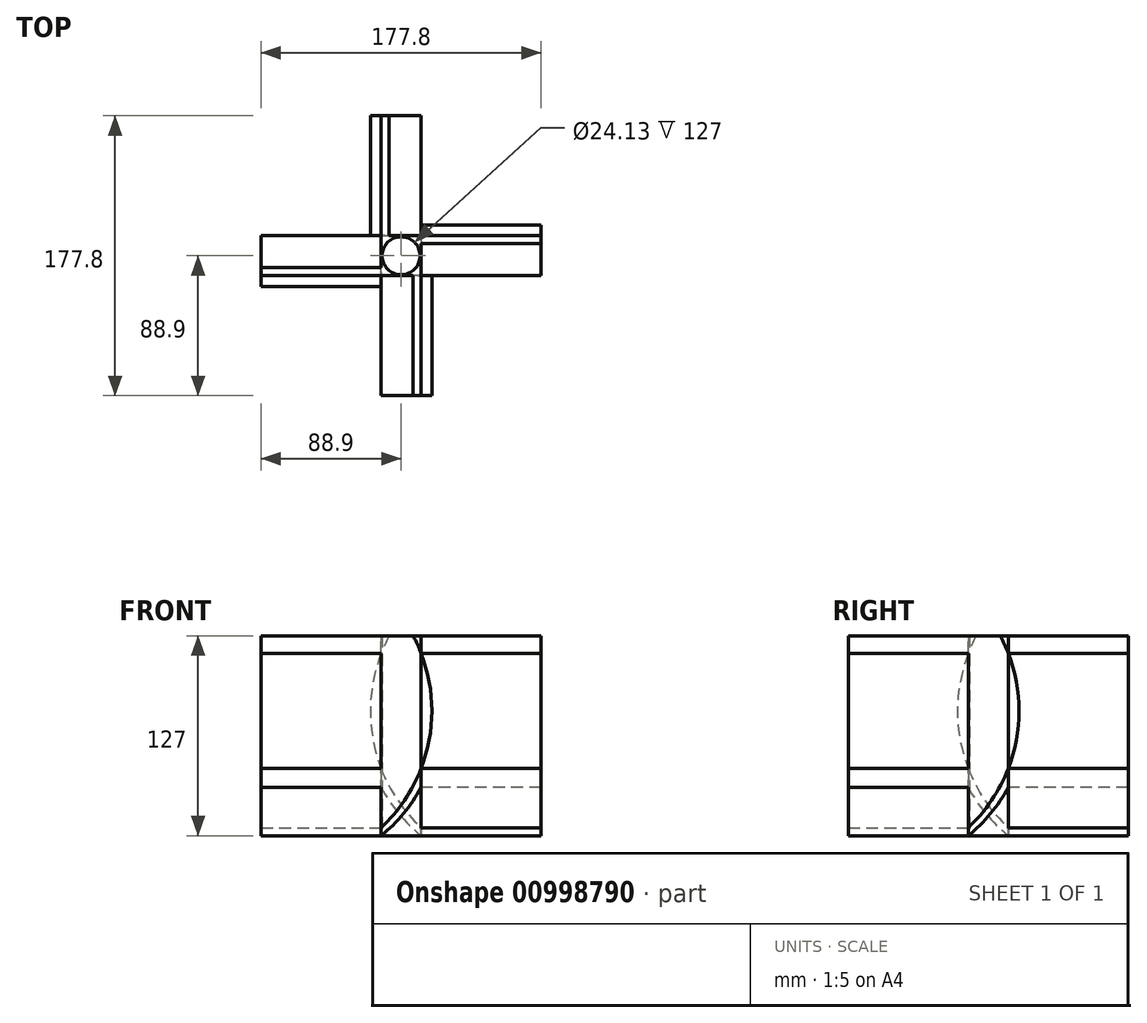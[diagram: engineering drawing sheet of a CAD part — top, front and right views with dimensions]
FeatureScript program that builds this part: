
annotation { "Feature Type Name" : "Feature", "Feature Type Description" : "" }
export const myFeature = defineFeature(function(context is Context, id is Id, definition is map)
    precondition{}
    {
        {
            var Q0;
            Q0=qCreatedBy(makeId("Top.planeOp"),FACE);
            var sketch = newSketch(context, id + "F0", { "sketchPlane" : qUnion([Q0])});
            skCircle(sketch, "E0", {"center": v(0, 0) * mm, "radius": 12.07 * mm});
            skLineSegment(sketch, "E1.bottom", {"start": v(12.7, -12.7) * mm, "end": v(-12.7, -12.7) * mm});
            skLineSegment(sketch, "E1.top", {"start": v(12.7, 12.7) * mm, "end": v(-12.7, 12.7) * mm});
            skLineSegment(sketch, "E1.left", {"start": v(12.7, -12.7) * mm, "end": v(12.7, 12.7) * mm});
            skLineSegment(sketch, "E1.right", {"start": v(-12.7, -12.7) * mm, "end": v(-12.7, 12.7) * mm});
            skSolve(sketch);
        }
        {
            var Q0;
            {var subQ0=sQuery(id+"F0.wireOp",EDGE,"E1.top");var subQ1=sQuery(id+"F0.wireOp",EDGE,"E0");var subQ2=makeQuery(id+"F0.imprint","INTERSECT",VERTEX,{"derivedFrom":[subQ1,subQ0]});Q0=makeQuery(id+"F0.imprint","IMPRINT",FACE,{"disambiguationData":[TD([[makeQuery(id+"F0.imprint","IMPRINT",EDGE,{"disambiguationData":[TD([[subQ2,1.0]])],"derivedFrom":subQ1}),-1.0]])]});}
            var Q1;
            {var subQ0=sQuery(id+"F0.wireOp",EDGE,"E1.top");var subQ1=sQuery(id+"F0.wireOp",EDGE,"E0");var subQ2=makeQuery(id+"F0.imprint","INTERSECT",VERTEX,{"derivedFrom":[subQ1,subQ0]});Q1=makeQuery(id+"F0.imprint","IMPRINT",FACE,{"disambiguationData":[TD([[makeQuery(id+"F0.imprint","IMPRINT",EDGE,{"disambiguationData":[TD([[subQ2,-1.0]])],"derivedFrom":subQ1}),-1.0]])]});}
            var Q2;
            {var subQ0=sQuery(id+"F0.wireOp",EDGE,"E1.right");var subQ1=sQuery(id+"F0.wireOp",EDGE,"E0");var subQ2=makeQuery(id+"F0.imprint","INTERSECT",VERTEX,{"derivedFrom":[subQ1,subQ0]});Q2=makeQuery(id+"F0.imprint","IMPRINT",FACE,{"disambiguationData":[TD([[makeQuery(id+"F0.imprint","IMPRINT",EDGE,{"disambiguationData":[TD([[subQ2,-1.0]])],"derivedFrom":subQ1}),-1.0]])]});}
            var Q3;
            {var subQ0=sQuery(id+"F0.wireOp",EDGE,"E1.left");var subQ1=sQuery(id+"F0.wireOp",EDGE,"E0");var subQ2=makeQuery(id+"F0.imprint","INTERSECT",VERTEX,{"derivedFrom":[subQ1,subQ0]});Q3=makeQuery(id+"F0.imprint","IMPRINT",FACE,{"disambiguationData":[TD([[makeQuery(id+"F0.imprint","IMPRINT",EDGE,{"disambiguationData":[TD([[subQ2,1.0]])],"derivedFrom":subQ1}),-1.0]])]});}
            extrude(context, id + "F1", {"entities" : qUnion([Q0, Q1, Q2, Q3]), "depth" : 127 * mm, "offsetDistance" : 25.4 * mm});
        }
        {
            var Q0;
            Q0=makeQuery(id+"F1.opExtrude","SWEPT_FACE",FACE,{"disambiguationData":[OSD([sQuery(id+"F0.wireOp",EDGE,"E1.left")])]});
            var sketch = newSketch(context, id + "F2", { "sketchPlane" : qUnion([Q0])});
            skArc(sketch, "E2", {"start": v(-12.7, 0) * mm, "mid": v(22.86, 58.93) * mm, "end": v(12.7, 127) * mm});
            skArc(sketch, "E3", {"start": v(-12.7, 5.08) * mm, "mid": v(18.13, 62.6) * mm, "end": v(7.62, 127) * mm});
            skLineSegment(sketch, "E4", {"start": v(-12.7, 5.08) * mm, "end": v(-12.7, 0) * mm});
            skLineSegment(sketch, "E5", {"start": v(7.62, 127) * mm, "end": v(12.7, 127) * mm});
            skSolve(sketch);
        }
        {
            var Q0;
            Q0=makeQuery(id+"Fi4T5MNTj5UxTLA_1.boolean.opBoolean","MERGE",FACE,{"derivedFrom":[makeQuery(id+"F1.opExtrude","SWEPT_FACE",FACE,{"disambiguationData":[OSD([sQuery(id+"F0.wireOp",EDGE,"E1.bottom")])]}),makeQuery(id+"Fi4T5MNTj5UxTLA_1.opExtrude","SWEPT_FACE",FACE,{"disambiguationData":[OSD([sQuery(id+"F2.wireOp",EDGE,"E4")])]})]});
            var sketch = newSketch(context, id + "F3", { "sketchPlane" : qUnion([Q0])});
            skArc(sketch, "E6", {"start": v(-12.7, 0) * mm, "mid": v(22.86, 58.93) * mm, "end": v(12.7, 127) * mm});
            skArc(sketch, "E7", {"start": v(-12.7, 5.08) * mm, "mid": v(18.13, 62.6) * mm, "end": v(7.62, 127) * mm});
            skSolve(sketch);
        }
        {
            var Q0;
            Q0=makeQuery(id+"F1.opExtrude","SWEPT_FACE",FACE,{"disambiguationData":[OSD([sQuery(id+"F0.wireOp",EDGE,"E1.right")])]});
            var sketch = newSketch(context, id + "F4", { "sketchPlane" : qUnion([Q0])});
            skArc(sketch, "E8", {"start": v(-12.7, 5.08) * mm, "mid": v(18.13, 62.6) * mm, "end": v(7.62, 127) * mm});
            skArc(sketch, "E9", {"start": v(-12.7, 0) * mm, "mid": v(22.86, 58.93) * mm, "end": v(12.7, 127) * mm});
            skSolve(sketch);
        }
        {
            var Q0;
            Q0=makeQuery(id+"F1.opExtrude","SWEPT_FACE",FACE,{"disambiguationData":[OSD([sQuery(id+"F0.wireOp",EDGE,"E1.top")])]});
            var sketch = newSketch(context, id + "F5", { "sketchPlane" : qUnion([Q0])});
            skArc(sketch, "E10", {"start": v(-12.7, 0) * mm, "mid": v(22.86, 58.93) * mm, "end": v(12.7, 127) * mm});
            skArc(sketch, "E11", {"start": v(-12.7, 5.08) * mm, "mid": v(18.13, 62.6) * mm, "end": v(7.62, 127) * mm});
            skSolve(sketch);
        }
        {
            var Q0;
            {var subQ0=sQuery(id+"F2.wireOp",EDGE,"E4");Q0=makeQuery(id+"F2.imprint","IMPRINT",FACE,{"disambiguationData":[TD([[makeQuery(id+"F2.imprint","IMPRINT",EDGE,{"derivedFrom":subQ0}),1.0]])]});}
            var Q1;
            {var subQ0=sQuery(id+"F2.wireOp",EDGE,"E3");var subQ1=makeQuery(id+"F1.opExtrude","SWEPT_EDGE",EDGE,{"disambiguationData":[OSD([sQuery(id+"F0.wireOp",EDGE,"E1.top"),sQuery(id+"F0.wireOp",EDGE,"E1.left")])]});var subQ2=makeQuery(id+"F2.imprint","INTERSECT",VERTEX,{"disambiguationData":[OD(0.0)],"derivedFrom":[subQ1,subQ0]});Q1=makeQuery(id+"F2.imprint","IMPRINT",FACE,{"disambiguationData":[TD([[makeQuery(id+"F2.imprint","IMPRINT",EDGE,{"disambiguationData":[TD([[subQ2,-1.0]])],"derivedFrom":subQ0}),1.0]])]});}
            var Q2;
            {var subQ0=sQuery(id+"F2.wireOp",EDGE,"E5");Q2=makeQuery(id+"F2.imprint","IMPRINT",FACE,{"disambiguationData":[TD([[makeQuery(id+"F2.imprint","IMPRINT",EDGE,{"derivedFrom":subQ0}),-1.0]])]});}
            extrude(context, id + "F6", {"entities" : qUnion([Q0, Q1, Q2]), "operationType" : NewBodyOperationType.ADD, "depth" : 76.2 * mm, "offsetDistance" : 25.4 * mm});
        }
        {
            var Q0;
            {var subQ1=sQuery(id+"F0.wireOp",EDGE,"E1.bottom");var subQ2=makeQuery(id+"F1.opExtrude","SWEPT_EDGE",EDGE,{"disambiguationData":[OSD([subQ1,sQuery(id+"F0.wireOp",EDGE,"E1.right")])]});var subQ6=sQuery(id+"F3.wireOp",EDGE,"E7");var subQ7=makeQuery(id+"F3.imprint","INTERSECT",VERTEX,{"derivedFrom":[subQ2,subQ6]});Q0=makeQuery(id+"F3.imprint","IMPRINT",FACE,{"disambiguationData":[TD([[makeQuery(id+"F3.imprint","IMPRINT",EDGE,{"disambiguationData":[TD([[subQ7,-1.0]])],"derivedFrom":subQ6}),-1.0]])]});}
            var Q1;
            {var subQ0=sQuery(id+"F3.wireOp",EDGE,"E7");var subQ1=makeQuery(id+"F1.opExtrude","SWEPT_EDGE",EDGE,{"disambiguationData":[OSD([sQuery(id+"F0.wireOp",EDGE,"E1.bottom"),sQuery(id+"F0.wireOp",EDGE,"E1.left")])]});var subQ2=makeQuery(id+"F3.imprint","INTERSECT",VERTEX,{"disambiguationData":[OD(0.0)],"derivedFrom":[subQ1,subQ0]});Q1=makeQuery(id+"F3.imprint","IMPRINT",FACE,{"disambiguationData":[TD([[makeQuery(id+"F3.imprint","IMPRINT",EDGE,{"disambiguationData":[TD([[subQ2,-1.0]])],"derivedFrom":subQ0}),1.0]])]});}
            var Q2;
            {var subQ0=sQuery(id+"F3.wireOp",EDGE,"E7");var subQ1=sQuery(id+"F0.wireOp",EDGE,"E1.bottom");var subQ2=makeQuery(id+"F1.opExtrude","CAP_EDGE",EDGE,{"disambiguationData":[OSD([subQ1])],"isStart":false});var subQ3=makeQuery(id+"F3.imprint","INTERSECT",VERTEX,{"derivedFrom":[subQ2,subQ0]});Q2=makeQuery(id+"F3.imprint","IMPRINT",FACE,{"disambiguationData":[TD([[makeQuery(id+"F3.imprint","IMPRINT",EDGE,{"disambiguationData":[TD([[subQ3,1.0]])],"derivedFrom":subQ0}),-1.0]])]});}
            extrude(context, id + "F7", {"entities" : qUnion([Q0, Q1, Q2]), "operationType" : NewBodyOperationType.ADD, "depth" : 76.2 * mm, "offsetDistance" : 25.4 * mm});
        }
        {
            var Q0;
            {var subQ0=sQuery(id+"F4.wireOp",EDGE,"E8");var subQ1=sQuery(id+"F0.wireOp",EDGE,"E1.right");var subQ2=makeQuery(id+"F1.opExtrude","SWEPT_EDGE",EDGE,{"disambiguationData":[OSD([sQuery(id+"F0.wireOp",EDGE,"E1.top"),subQ1])]});var subQ3=makeQuery(id+"F4.imprint","INTERSECT",VERTEX,{"derivedFrom":[subQ2,subQ0]});Q0=makeQuery(id+"F4.imprint","IMPRINT",FACE,{"disambiguationData":[TD([[makeQuery(id+"F4.imprint","IMPRINT",EDGE,{"disambiguationData":[TD([[subQ3,-1.0]])],"derivedFrom":subQ0}),-1.0]])]});}
            var Q1;
            {var subQ0=sQuery(id+"F4.wireOp",EDGE,"E8");var subQ1=makeQuery(id+"F1.opExtrude","SWEPT_EDGE",EDGE,{"disambiguationData":[OSD([sQuery(id+"F0.wireOp",EDGE,"E1.bottom"),sQuery(id+"F0.wireOp",EDGE,"E1.right")])]});var subQ2=makeQuery(id+"F4.imprint","INTERSECT",VERTEX,{"disambiguationData":[OD(0.0)],"derivedFrom":[subQ1,subQ0]});Q1=makeQuery(id+"F4.imprint","IMPRINT",FACE,{"disambiguationData":[TD([[makeQuery(id+"F4.imprint","IMPRINT",EDGE,{"disambiguationData":[TD([[subQ2,-1.0]])],"derivedFrom":subQ0}),1.0]])]});}
            var Q2;
            {var subQ0=sQuery(id+"F4.wireOp",EDGE,"E8");var subQ1=sQuery(id+"F0.wireOp",EDGE,"E1.right");var subQ2=makeQuery(id+"F1.opExtrude","CAP_EDGE",EDGE,{"disambiguationData":[OSD([subQ1])],"isStart":false});var subQ3=makeQuery(id+"F4.imprint","INTERSECT",VERTEX,{"derivedFrom":[subQ2,subQ0]});Q2=makeQuery(id+"F4.imprint","IMPRINT",FACE,{"disambiguationData":[TD([[makeQuery(id+"F4.imprint","IMPRINT",EDGE,{"disambiguationData":[TD([[subQ3,1.0]])],"derivedFrom":subQ0}),-1.0]])]});}
            extrude(context, id + "F8", {"entities" : qUnion([Q0, Q1, Q2]), "operationType" : NewBodyOperationType.ADD, "depth" : 76.2 * mm, "offsetDistance" : 25.4 * mm});
        }
        {
            var Q0;
            {var subQ1=sQuery(id+"F0.wireOp",EDGE,"E1.top");var subQ2=makeQuery(id+"F1.opExtrude","SWEPT_EDGE",EDGE,{"disambiguationData":[OSD([subQ1,sQuery(id+"F0.wireOp",EDGE,"E1.left")])]});var subQ6=sQuery(id+"F5.wireOp",EDGE,"E11");var subQ7=makeQuery(id+"F5.imprint","INTERSECT",VERTEX,{"derivedFrom":[subQ2,subQ6]});Q0=makeQuery(id+"F5.imprint","IMPRINT",FACE,{"disambiguationData":[TD([[makeQuery(id+"F5.imprint","IMPRINT",EDGE,{"disambiguationData":[TD([[subQ7,-1.0]])],"derivedFrom":subQ6}),-1.0]])]});}
            var Q1;
            {var subQ0=sQuery(id+"F5.wireOp",EDGE,"E11");var subQ1=makeQuery(id+"F1.opExtrude","SWEPT_EDGE",EDGE,{"disambiguationData":[OSD([sQuery(id+"F0.wireOp",EDGE,"E1.top"),sQuery(id+"F0.wireOp",EDGE,"E1.right")])]});var subQ2=makeQuery(id+"F5.imprint","INTERSECT",VERTEX,{"disambiguationData":[OD(0.0)],"derivedFrom":[subQ1,subQ0]});Q1=makeQuery(id+"F5.imprint","IMPRINT",FACE,{"disambiguationData":[TD([[makeQuery(id+"F5.imprint","IMPRINT",EDGE,{"disambiguationData":[TD([[subQ2,-1.0]])],"derivedFrom":subQ0}),1.0]])]});}
            var Q2;
            {var subQ0=sQuery(id+"F5.wireOp",EDGE,"E11");var subQ1=sQuery(id+"F0.wireOp",EDGE,"E1.top");var subQ2=makeQuery(id+"F1.opExtrude","CAP_EDGE",EDGE,{"disambiguationData":[OSD([subQ1])],"isStart":false});var subQ3=makeQuery(id+"F5.imprint","INTERSECT",VERTEX,{"derivedFrom":[subQ2,subQ0]});Q2=makeQuery(id+"F5.imprint","IMPRINT",FACE,{"disambiguationData":[TD([[makeQuery(id+"F5.imprint","IMPRINT",EDGE,{"disambiguationData":[TD([[subQ3,1.0]])],"derivedFrom":subQ0}),-1.0]])]});}
            extrude(context, id + "F9", {"entities" : qUnion([Q0, Q1, Q2]), "operationType" : NewBodyOperationType.ADD, "depth" : 76.2 * mm, "offsetDistance" : 25.4 * mm});
        }
    });
